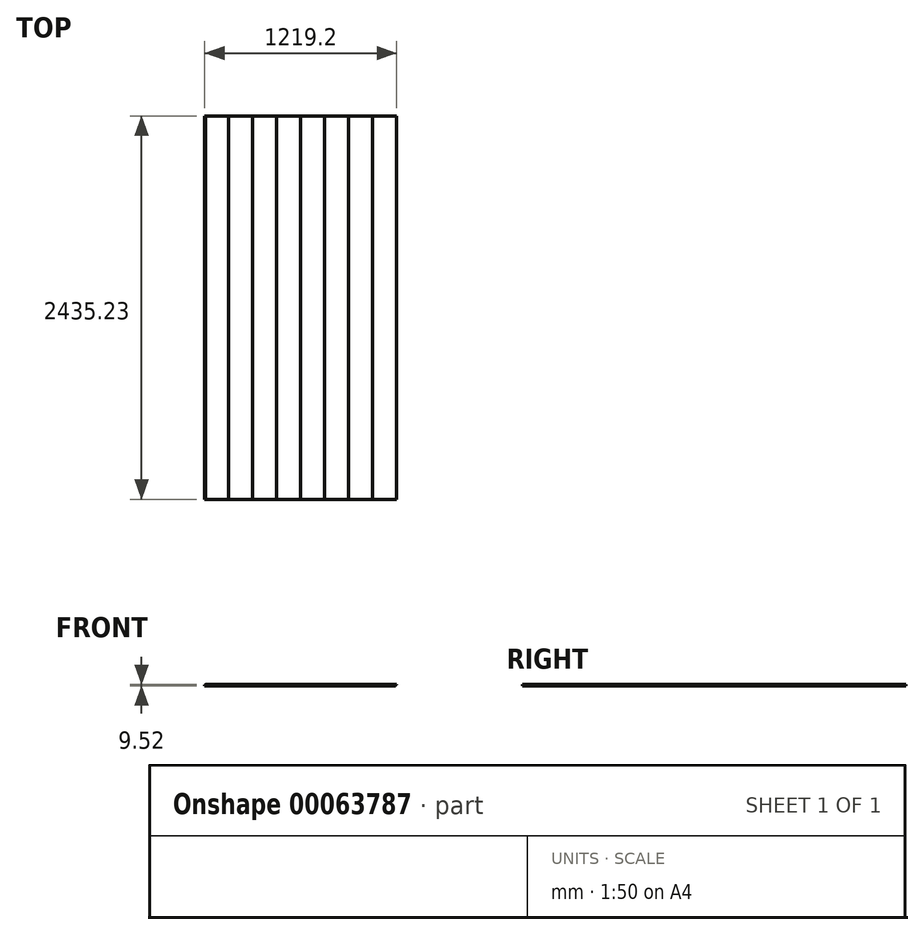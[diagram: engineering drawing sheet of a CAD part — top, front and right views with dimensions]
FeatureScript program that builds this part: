
annotation { "Feature Type Name" : "Feature", "Feature Type Description" : "" }
export const myFeature = defineFeature(function(context is Context, id is Id, definition is map)
    precondition{}
    {
        {
            var Q0;
            Q0=qCreatedBy(makeId("Top.planeOp"),FACE);
            var sketch = newSketch(context, id + "F0", { "sketchPlane" : qUnion([Q0])});
            skLineSegment(sketch, "E0.bottom", {"start": v(-609.6, 1911.45) * mm, "end": v(609.6, 1911.45) * mm});
            skLineSegment(sketch, "E0.top", {"start": v(-609.6, -523.78) * mm, "end": v(609.6, -523.78) * mm});
            skLineSegment(sketch, "E0.left", {"start": v(-609.6, 1911.45) * mm, "end": v(-609.6, -523.78) * mm});
            skLineSegment(sketch, "E0.right", {"start": v(609.6, 1911.45) * mm, "end": v(609.6, -523.78) * mm});
            skSolve(sketch);
        }
        {
            var Q0;
            Q0=qSketchRegion(id+"F0",true);
            extrude(context, id + "F1", {"entities" : qUnion([Q0]), "endBound" : BoundingType.SYMMETRIC, "depth" : 9.52 * mm});
        }
        {
            var Q0;
            Q0=makeQuery(id+"F1.opExtrude","SWEPT_FACE",FACE,{"disambiguationData":[OSD([sQuery(id+"F0.wireOp",EDGE,"E0.top")])]});
            var sketch = newSketch(context, id + "F2", { "sketchPlane" : qUnion([Q0])});
            skLineSegment(sketch, "E1", {"start": v(609.6, 0) * mm, "end": v(603.25, 0) * mm});
            skPoint(sketch, "E1.endSnap0", {"position": v(609.6, 0) * mm});
            skLineSegment(sketch, "E2", {"start": v(603.25, 0) * mm, "end": v(603.25, -4.76) * mm});
            skLineSegment(sketch, "E3", {"start": v(609.6, 0) * mm, "end": v(609.6, -4.76) * mm});
            skLineSegment(sketch, "E4", {"start": v(609.6, -4.76) * mm, "end": v(603.25, -4.76) * mm});
            skLineSegment(sketch, "E5.bottom", {"start": v(-609.6, 4.76) * mm, "end": v(-603.25, 4.76) * mm});
            skLineSegment(sketch, "E5.top", {"start": v(-609.6, 0) * mm, "end": v(-603.25, 0) * mm});
            skLineSegment(sketch, "E5.left", {"start": v(-609.6, 4.76) * mm, "end": v(-609.6, 0) * mm});
            skLineSegment(sketch, "E5.right", {"start": v(-603.25, 4.76) * mm, "end": v(-603.25, 0) * mm});
            skSolve(sketch);
        }
        {
            var Q0;
            Q0 = qSketchRegion(id + "F2", true);
            extrude(context, id + "F3", {"entities" : qUnion([Q0]), "operationType" : NewBodyOperationType.REMOVE, "endBound" : BoundingType.THROUGH_ALL, "oppositeDirection" : true, "depth" : 25.4 * mm});
        }
        {
            var Q0;
            Q0=makeQuery(id+"F1.opExtrude","SWEPT_FACE",FACE,{"disambiguationData":[OSD([sQuery(id+"F0.wireOp",EDGE,"E0.top")])]});
            var sketch = newSketch(context, id + "F4", { "sketchPlane" : qUnion([Q0])});
            skLineSegment(sketch, "E6.bottom", {"start": v(-458, 4.76) * mm, "end": v(-456.4, 4.76) * mm});
            skLineSegment(sketch, "E6.top", {"start": v(-458, 3.17) * mm, "end": v(-456.4, 3.17) * mm});
            skLineSegment(sketch, "E6.left", {"start": v(-458, 4.76) * mm, "end": v(-458, 3.17) * mm});
            skLineSegment(sketch, "E6.right", {"start": v(-456.4, 4.76) * mm, "end": v(-456.4, 3.17) * mm});
            skPoint(sketch, "E7", {"position": v(-457.2, 3.17) * mm});
            skPoint(sketch, "E8.1.0.0", {"position": v(-304.8, 3.17) * mm});
            skLineSegment(sketch, "E8.1.0.1", {"start": v(-305.6, 4.76) * mm, "end": v(-304, 4.76) * mm});
            skLineSegment(sketch, "E8.1.0.2", {"start": v(-305.6, 3.17) * mm, "end": v(-304, 3.17) * mm});
            skLineSegment(sketch, "E8.1.0.3", {"start": v(-305.6, 4.76) * mm, "end": v(-305.6, 3.17) * mm});
            skLineSegment(sketch, "E8.1.0.4", {"start": v(-304, 4.76) * mm, "end": v(-304, 3.17) * mm});
            skPoint(sketch, "E8.2.0.0", {"position": v(-152.4, 3.17) * mm});
            skLineSegment(sketch, "E8.2.0.1", {"start": v(-153.2, 4.76) * mm, "end": v(-151.6, 4.76) * mm});
            skLineSegment(sketch, "E8.2.0.2", {"start": v(-153.2, 3.17) * mm, "end": v(-151.6, 3.17) * mm});
            skLineSegment(sketch, "E8.2.0.3", {"start": v(-153.2, 4.76) * mm, "end": v(-153.2, 3.17) * mm});
            skLineSegment(sketch, "E8.2.0.4", {"start": v(-151.6, 4.76) * mm, "end": v(-151.6, 3.17) * mm});
            skPoint(sketch, "E8.3.0.0", {"position": v(0, 3.17) * mm});
            skLineSegment(sketch, "E8.3.0.1", {"start": v(-0.8, 4.76) * mm, "end": v(0.8, 4.76) * mm});
            skLineSegment(sketch, "E8.3.0.2", {"start": v(-0.8, 3.17) * mm, "end": v(0.8, 3.17) * mm});
            skLineSegment(sketch, "E8.3.0.3", {"start": v(-0.8, 4.76) * mm, "end": v(-0.8, 3.17) * mm});
            skLineSegment(sketch, "E8.3.0.4", {"start": v(0.8, 4.76) * mm, "end": v(0.8, 3.17) * mm});
            skPoint(sketch, "E8.4.0.0", {"position": v(152.4, 3.17) * mm});
            skLineSegment(sketch, "E8.4.0.1", {"start": v(151.6, 4.76) * mm, "end": v(153.2, 4.76) * mm});
            skLineSegment(sketch, "E8.4.0.2", {"start": v(151.6, 3.17) * mm, "end": v(153.2, 3.17) * mm});
            skLineSegment(sketch, "E8.4.0.3", {"start": v(151.6, 4.76) * mm, "end": v(151.6, 3.17) * mm});
            skLineSegment(sketch, "E8.4.0.4", {"start": v(153.2, 4.76) * mm, "end": v(153.2, 3.17) * mm});
            skPoint(sketch, "E8.5.0.0", {"position": v(304.8, 3.17) * mm});
            skLineSegment(sketch, "E8.5.0.1", {"start": v(304, 4.76) * mm, "end": v(305.6, 4.76) * mm});
            skLineSegment(sketch, "E8.5.0.2", {"start": v(304, 3.17) * mm, "end": v(305.6, 3.17) * mm});
            skLineSegment(sketch, "E8.5.0.3", {"start": v(304, 4.76) * mm, "end": v(304, 3.17) * mm});
            skLineSegment(sketch, "E8.5.0.4", {"start": v(305.6, 4.76) * mm, "end": v(305.6, 3.17) * mm});
            skPoint(sketch, "E8.6.0.0", {"position": v(457.2, 3.17) * mm});
            skLineSegment(sketch, "E8.6.0.1", {"start": v(456.4, 4.76) * mm, "end": v(458, 4.76) * mm});
            skLineSegment(sketch, "E8.6.0.2", {"start": v(456.4, 3.17) * mm, "end": v(458, 3.17) * mm});
            skLineSegment(sketch, "E8.6.0.3", {"start": v(456.4, 4.76) * mm, "end": v(456.4, 3.17) * mm});
            skLineSegment(sketch, "E8.6.0.4", {"start": v(458, 4.76) * mm, "end": v(458, 3.17) * mm});
            skLineSegment(sketch, "E8.direction1", {"start": v(-457.2, 3.17) * mm, "end": v(-304.8, 3.17) * mm, "construction": true});
            skSolve(sketch);
        }
        {
            var Q0;
            Q0 = qSketchRegion(id + "F4", true);
            extrude(context, id + "F5", {"entities" : qUnion([Q0]), "operationType" : NewBodyOperationType.REMOVE, "endBound" : BoundingType.THROUGH_ALL, "oppositeDirection" : true, "depth" : 25.4 * mm});
        }
    });
